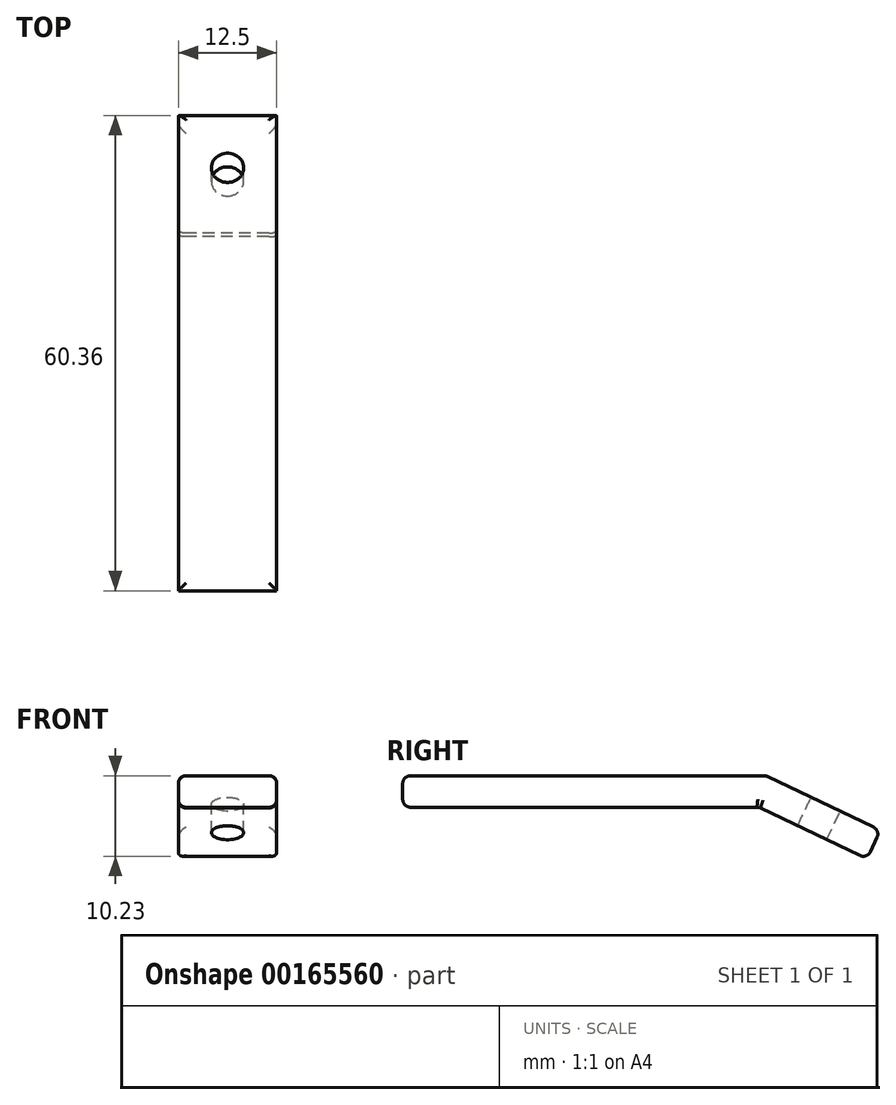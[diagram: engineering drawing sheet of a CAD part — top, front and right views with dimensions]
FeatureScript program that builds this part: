
annotation { "Feature Type Name" : "Feature", "Feature Type Description" : "" }
export const myFeature = defineFeature(function(context is Context, id is Id, definition is map)
    precondition{}
    {
        {
            var Q0;
            Q0=qCreatedBy(makeId("Right.planeOp"),FACE);
            var sketch = newSketch(context, id + "F0", { "sketchPlane" : qUnion([Q0])});
            skLineSegment(sketch, "E0", {"start": v(0, 0) * mm, "end": v(-45, 0) * mm});
            skLineSegment(sketch, "E1", {"start": v(0.43, -0.1) * mm, "end": v(13.97, -6.57) * mm});
            skLineSegment(sketch, "E2.0", {"start": v(1.13, 4) * mm, "end": v(-45, 4) * mm});
            skLineSegment(sketch, "E2.1", {"start": v(1.13, 4) * mm, "end": v(15.69, -2.96) * mm});
            skLineSegment(sketch, "E3", {"start": v(15.69, -2.96) * mm, "end": v(13.97, -6.57) * mm});
            skLineSegment(sketch, "E4", {"start": v(-45, 4) * mm, "end": v(-45, 0) * mm});
            skLineSegment(sketch, "E5", {"start": v(0, 0) * mm, "end": v(0.43, -0.1) * mm});
            skSolve(sketch);
        }
        {
            var Q0;
            Q0=makeQuery(id+"F0.imprint","IMPRINT",FACE,{"disambiguationData":[TD([[makeQuery(id+"F0.imprint","IMPRINT",EDGE,{"derivedFrom":sQuery(id+"F0.wireOp",EDGE,"E0")}),-1.0]])]});
            extrude(context, id + "F1", {"entities" : qUnion([Q0]), "depth" : 12.5 * mm});
        }
        {
            var Q0;
            Q0=makeQuery(id+"F1.opExtrude","SWEPT_FACE",FACE,{"disambiguationData":[OSD([sQuery(id+"F0.wireOp",EDGE,"E2.1")])]});
            var sketch = newSketch(context, id + "F2", { "sketchPlane" : qUnion([Q0])});
            skCircle(sketch, "E6", {"center": v(6.25, 7.72) * mm, "radius": 2.05 * mm});
            skSolve(sketch);
        }
        {
            var Q0;
            Q0=qSketchRegion(id+"F2",true);
            extrude(context, id + "F3", {"entities" : qUnion([Q0]), "operationType" : NewBodyOperationType.REMOVE, "oppositeDirection" : true, "depth" : 25 * mm});
        }
        {
            var Q0;
            Q0=makeQuery(id+"F1.opExtrude","SWEPT_FACE",FACE,{"disambiguationData":[OSD([sQuery(id+"F0.wireOp",EDGE,"E2.0")])]});
            var Q1;
            Q1=makeQuery(id+"F1.opExtrude","CAP_EDGE",EDGE,{"disambiguationData":[OSD([sQuery(id+"F0.wireOp",EDGE,"E2.1")])],"isStart":false});
            var Q2;
            Q2=makeQuery(id+"F1.opExtrude","SWEPT_EDGE",EDGE,{"disambiguationData":[OSD([sQuery(id+"F0.wireOp",EDGE,"E2.1"),sQuery(id+"F0.wireOp",EDGE,"E3")])]});
            var Q3;
            Q3=makeQuery(id+"F1.opExtrude","CAP_EDGE",EDGE,{"disambiguationData":[OSD([sQuery(id+"F0.wireOp",EDGE,"E2.1")])],"isStart":true});
            var Q4;
            Q4=makeQuery(id+"F1.opExtrude","CAP_EDGE",EDGE,{"disambiguationData":[OSD([sQuery(id+"F0.wireOp",EDGE,"E0")])],"isStart":false});
            var Q5;
            Q5=makeQuery(id+"F1.opExtrude","CAP_EDGE",EDGE,{"disambiguationData":[OSD([sQuery(id+"F0.wireOp",EDGE,"E0")])],"isStart":true});
            var Q6;
            Q6=makeQuery(id+"F1.opExtrude","SWEPT_EDGE",EDGE,{"disambiguationData":[OSD([sQuery(id+"F0.wireOp",EDGE,"E0"),sQuery(id+"F0.wireOp",EDGE,"E4")])]});
            var Q7;
            Q7=makeQuery(id+"F1.opExtrude","CAP_EDGE",EDGE,{"disambiguationData":[OSD([sQuery(id+"F0.wireOp",EDGE,"E1")])],"isStart":false});
            var Q8;
            Q8=makeQuery(id+"F1.opExtrude","CAP_EDGE",EDGE,{"disambiguationData":[OSD([sQuery(id+"F0.wireOp",EDGE,"E1")])],"isStart":true});
            var Q9;
            Q9=makeQuery(id+"F1.opExtrude","SWEPT_EDGE",EDGE,{"disambiguationData":[OSD([sQuery(id+"F0.wireOp",EDGE,"E1"),sQuery(id+"F0.wireOp",EDGE,"E3")])]});
            var Q10;
            Q10=makeQuery(id+"F1.opExtrude","CAP_EDGE",EDGE,{"disambiguationData":[OSD([sQuery(id+"F0.wireOp",EDGE,"E5")])],"isStart":false});
            var Q11;
            Q11=makeQuery(id+"F1.opExtrude","CAP_EDGE",EDGE,{"disambiguationData":[OSD([sQuery(id+"F0.wireOp",EDGE,"E5")])],"isStart":true});
            fillet(context, id + "F4", {"entities" : qUnion([Q0, Q1, Q2, Q3, Q4, Q5, Q6, Q7, Q8, Q9, Q10, Q11]), "radius" : 1 * mm, "tangentPropagation" : true, "allowEdgeOverflow" : false});
        }
    });
